# Revit family: Grohe_PlumbingFixture_Bauflow_SingleLeverBathMixer_23601000a
name_source: partatom
category: Plumbing Fixtures
revit_build: Autodesk Revit 2018 (Build: 20190510_1515(x64)
units: mm (PartAtom-declared; Revit-internal decimal feet)

## family parameters
Cut with Voids When Loaded = No
Host = Face
OmniClass Number = 23.65.00.00
OmniClass Title = Supply and Distribution of Liquids and Gases
Part Type = Normal
Room Calculation Point = No
Round Connector Dimension = Use Diameter
Shared = No

## types (1)
- 23601000
    ADACompliant = No
    Assembly Code = D2010
    AssetType = Fixed
    BIMObjectName = Grohe_PlumbingFixture_Bauflow_SingleLeverBathMixer_23601000
    CWFU = 4.5
    ClassificationName = Uniclass 2015
    ClassificationValue = Pr_40_20_87_07
    ColdWaterConnectionDiameter = 10 mm  [stored 0.0328084 ft]
    Color = Chrome
    Cost = 0 $
    Default Elevation = 0 mm  [stored 0 ft]
    DocumentationCertificates = www.grohe.co.uk/
    DocumentationInstallationGuide = www.grohe.co.uk/
    DocumentationLiterature = www.grohe.co.uk/
    DocumentationMaintenance = www.grohe.co.uk/
    DocumentationTechnical = www.grohe.co.uk/
    DurationUnit = Years
    Ecojoy = No
    ExpectedLife = 0
    FaucetMaterial = Grohe-Chrome
    Features = wall mounted
metal lever
GROHE Longlife 35 mm ceramic cartridge
GROHE StarLight chrome finish
automatic diverter: bath/shower
mousseur
S-unions
metal wall escutcheon
    HWFU = 4.5
    HotWaterConnectionDiameter = 10 mm  [stored 0.0328084 ft]
    IfcExportAs = IfcPipeFitting
    IfcExportType = IfcPipeFittingType
    Keynote = N13
    LowEmittingMaterial = No
    Manufacturer = Grohe
    ManufacturerName = Grohe
    MasterformatNumber = 01 52 19
    MasterformatTitle = Sanitary Facilities
    Model = BauFlow
    ModelNumber = 23601000
    ModelReference = BauFlow - Single-lever bath mixer 1/2″
    NBSDescription = Water supply fittings for baths
    NBSObjectName = Grohe - Water supply fittings for baths
    NBSReference = 45-35-70/315
    NominalDepth = 0 mm  [stored 0 ft]
    NominalHeight = 0 mm  [stored 0 ft]
    NominalLength = 0 mm  [stored 0 ft]
    ProductPageURL = https://www.grohe-gcc.com
    ProductionYear = 2020
    Type Comments = Single-lever bath mixer 1/2″
    TypeName = BauFlow - Single-lever bath mixer 1/2″
    URL = www.grohe.com
    WarrantyDurationLabor = 0
    WarrantyDurationParts = 0
    WarrantyDurationUnit = Years
    _BSBibleVersion = 16
    _BimSpecGuid = 0
    _CurrentRevision = 1
    _DistributedBy = www.bimstore.co
    _ObjectUserGuide = www.bimstore.co

note: [stored X ft] marks values corroborated as IEEE doubles in the binary element streams (Revit-internal decimal feet)

## geometry (parser evidence)
native form markers: Sweep x3
no freeform markers — native parametric forms only
